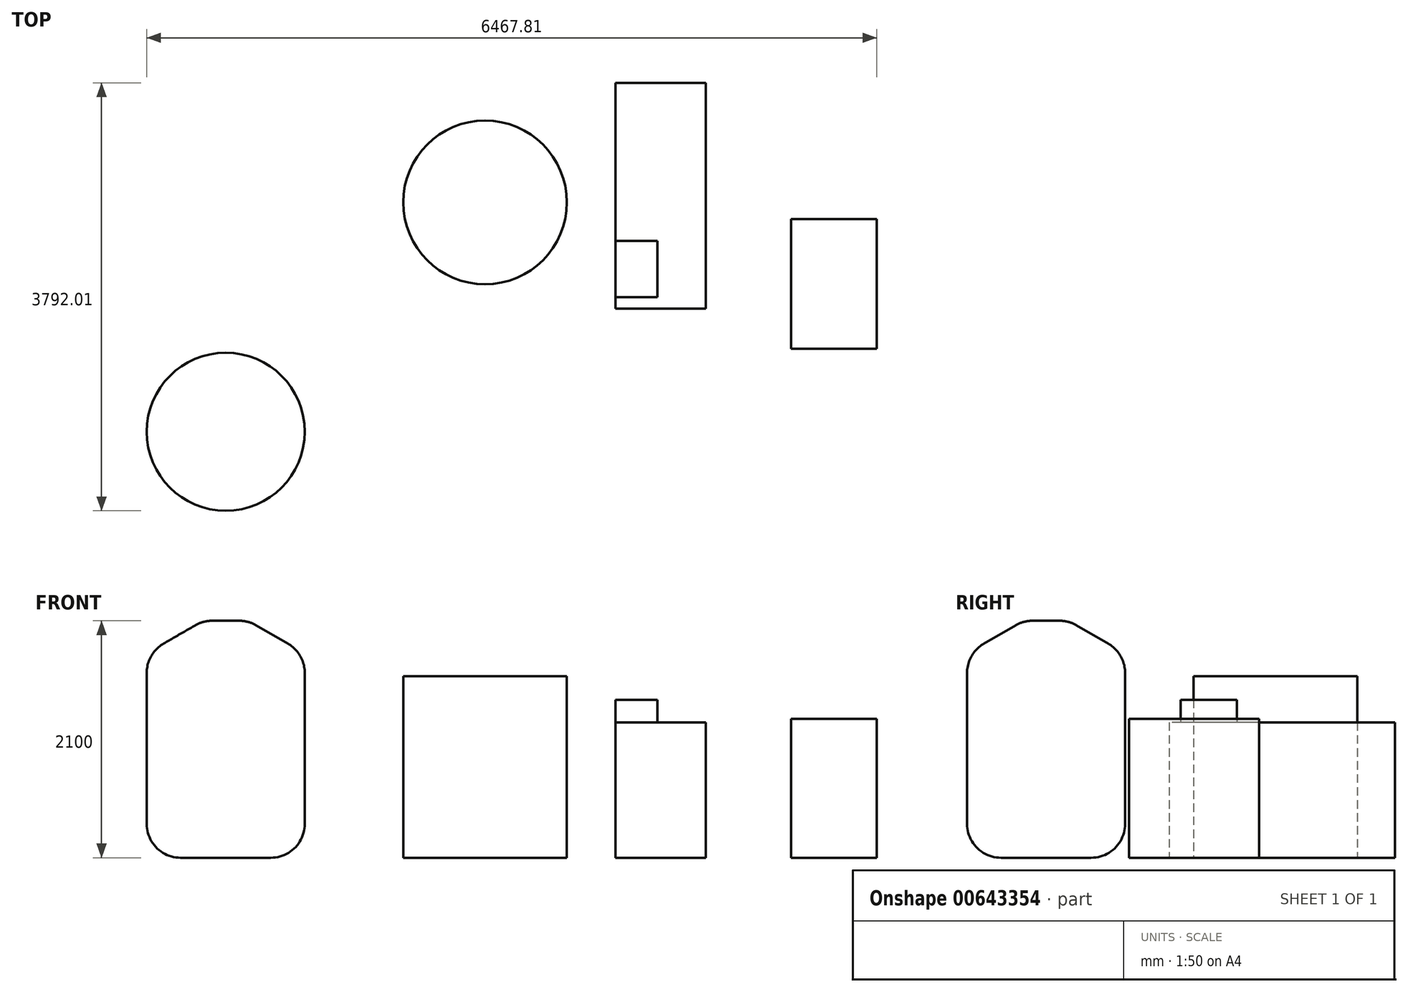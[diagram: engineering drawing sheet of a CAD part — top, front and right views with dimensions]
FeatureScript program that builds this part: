
annotation { "Feature Type Name" : "Feature", "Feature Type Description" : "" }
export const myFeature = defineFeature(function(context is Context, id is Id, definition is map)
    precondition{}
    {
        {
            var Q0;
            Q0=qCreatedBy(makeId("Top.planeOp"),FACE);
            var sketch = newSketch(context, id + "F0", { "sketchPlane" : qUnion([Q0])});
            skLineSegment(sketch, "E0.bottom", {"start": v(-411.47, -694.24) * mm, "end": v(348.53, -694.24) * mm});
            skLineSegment(sketch, "E0.top", {"start": v(-411.47, 455.76) * mm, "end": v(348.53, 455.76) * mm});
            skLineSegment(sketch, "E0.left", {"start": v(-411.47, -694.24) * mm, "end": v(-411.47, 455.76) * mm});
            skLineSegment(sketch, "E0.right", {"start": v(348.53, -694.24) * mm, "end": v(348.53, 455.76) * mm});
            skSolve(sketch);
        }
        {
            var Q0;
            Q0=qSketchRegion(id+"F0",true);
            extrude(context, id + "F1", {"entities" : qUnion([Q0]), "depth" : 1230 * mm, "offsetDistance" : 25 * mm});
        }
        {
            var Q0;
            Q0=qCreatedBy(makeId("Top.planeOp"),FACE);
            var sketch = newSketch(context, id + "F2", { "sketchPlane" : qUnion([Q0])});
            skCircle(sketch, "E1", {"center": v(-3121.8, 602.2) * mm, "radius": 725 * mm});
            skSolve(sketch);
        }
        {
            var Q0;
            Q0=makeQuery(id+"F2.imprint","IMPRINT",FACE,{"disambiguationData":[TD([[makeQuery(id+"F2.imprint","IMPRINT",EDGE,{"derivedFrom":sQuery(id+"F2.wireOp",EDGE,"E1")}),1.0]])]});
            extrude(context, id + "F3", {"entities" : qUnion([Q0]), "depth" : 1610 * mm, "offsetDistance" : 25 * mm});
        }
        {
            var Q0;
            Q0=qCreatedBy(makeId("Top.planeOp"),FACE);
            var sketch = newSketch(context, id + "F4", { "sketchPlane" : qUnion([Q0])});
            skLineSegment(sketch, "E2.bottom", {"start": v(-1964.82, 1661.78) * mm, "end": v(-1164.82, 1661.78) * mm});
            skLineSegment(sketch, "E2.top", {"start": v(-1964.82, -338.22) * mm, "end": v(-1164.82, -338.22) * mm});
            skLineSegment(sketch, "E2.left", {"start": v(-1964.82, 1661.78) * mm, "end": v(-1964.82, -338.22) * mm});
            skLineSegment(sketch, "E2.right", {"start": v(-1164.82, 1661.78) * mm, "end": v(-1164.82, -338.22) * mm});
            skSolve(sketch);
        }
        {
            var Q0;
            Q0=qSketchRegion(id+"F4",true);
            extrude(context, id + "F5", {"entities" : qUnion([Q0]), "depth" : 1200 * mm, "offsetDistance" : 25 * mm});
        }
        {
            var Q0;
            Q0=makeQuery(id+"F5.opExtrude","CAP_FACE",FACE,{"disambiguationData":[OSD([sQuery(id+"F4.wireOp",EDGE,"E2.bottom"),sQuery(id+"F4.wireOp",EDGE,"E2.top"),sQuery(id+"F4.wireOp",EDGE,"E2.left"),sQuery(id+"F4.wireOp",EDGE,"E2.right")])],"isStart":false});
            var sketch = newSketch(context, id + "F6", { "sketchPlane" : qUnion([Q0])});
            skLineSegment(sketch, "E3.bottom", {"start": v(-1594.82, 261.78) * mm, "end": v(-1964.82, 261.78) * mm});
            skLineSegment(sketch, "E3.top", {"start": v(-1594.82, -238.22) * mm, "end": v(-1964.82, -238.22) * mm});
            skLineSegment(sketch, "E3.left", {"start": v(-1594.82, 261.78) * mm, "end": v(-1594.82, -238.22) * mm});
            skLineSegment(sketch, "E3.right", {"start": v(-1964.82, 261.78) * mm, "end": v(-1964.82, -238.22) * mm});
            skSolve(sketch);
        }
        {
            var Q0;
            Q0=qSketchRegion(id+"F6",true);
            extrude(context, id + "F7", {"entities" : qUnion([Q0]), "operationType" : NewBodyOperationType.ADD, "depth" : 200 * mm, "offsetDistance" : 25 * mm});
        }
        {
            var Q0;
            Q0=qCreatedBy(makeId("Top.planeOp"),FACE);
            var sketch = newSketch(context, id + "F8", { "sketchPlane" : qUnion([Q0])});
            skCircle(sketch, "E4", {"center": v(-5419.28, -1430.23) * mm, "radius": 700 * mm});
            skSolve(sketch);
        }
        {
            var Q0;
            Q0=qSketchRegion(id+"F8",true);
            extrude(context, id + "F9", {"entities" : qUnion([Q0]), "depth" : 2100 * mm, "offsetDistance" : 25 * mm});
        }
        {
            var Q0;
            Q0=makeQuery(id+"F9.opExtrude","CAP_EDGE",EDGE,{"disambiguationData":[OSD([sQuery(id+"F8.wireOp",EDGE,"E4")])],"isStart":true});
            fillet(context, id + "F10", {"entities" : qUnion([Q0]), "radius" : 300 * mm, "tangentPropagation" : true, "allowEdgeOverflow" : false});
        }
        {
            var Q0;
            Q0=makeQuery(id+"F9.opExtrude","CAP_EDGE",EDGE,{"disambiguationData":[OSD([sQuery(id+"F8.wireOp",EDGE,"E4")])],"isStart":false});
            chamfer(context, id + "F11", {"entities" : qUnion([Q0]), "chamferType" : ChamferType.OFFSET_ANGLE, "width" : 500 * mm, "oppositeDirection" : false, "angle" : 30 * degree, "tangentPropagation" : true});
        }
        {
            var Q0;
            {var subQ0=sQuery(id+"F8.wireOp",EDGE,"E4");Q0=makeQuery(id+"F11.opChamfer","BLEND_EDGE",EDGE,{"blendedFrom":[makeQuery(id+"F9.opExtrude","CAP_EDGE",EDGE,{"disambiguationData":[OSD([subQ0])],"isStart":false}),makeQuery(id+"F9.opExtrude","SWEPT_FACE",FACE,{"disambiguationData":[OSD([subQ0])]})],"blendedInto":[makeQuery(id+"F9.opExtrude","SWEPT_FACE",FACE,{"disambiguationData":[OSD([subQ0])]})]});}
            var Q1;
            {var subQ0=sQuery(id+"F8.wireOp",EDGE,"E4");Q1=makeQuery(id+"F11.opChamfer","BLEND_EDGE",EDGE,{"blendedFrom":[makeQuery(id+"F9.opExtrude","CAP_EDGE",EDGE,{"disambiguationData":[OSD([subQ0])],"isStart":false}),makeQuery(id+"F9.opExtrude","CAP_FACE",FACE,{"disambiguationData":[OSD([subQ0])],"isStart":false})],"blendedInto":[makeQuery(id+"F9.opExtrude","CAP_FACE",FACE,{"disambiguationData":[OSD([subQ0])],"isStart":false})]});}
            fillet(context, id + "F12", {"entities" : qUnion([Q0, Q1]), "radius" : 300 * mm, "tangentPropagation" : true, "allowEdgeOverflow" : false});
        }
    });
